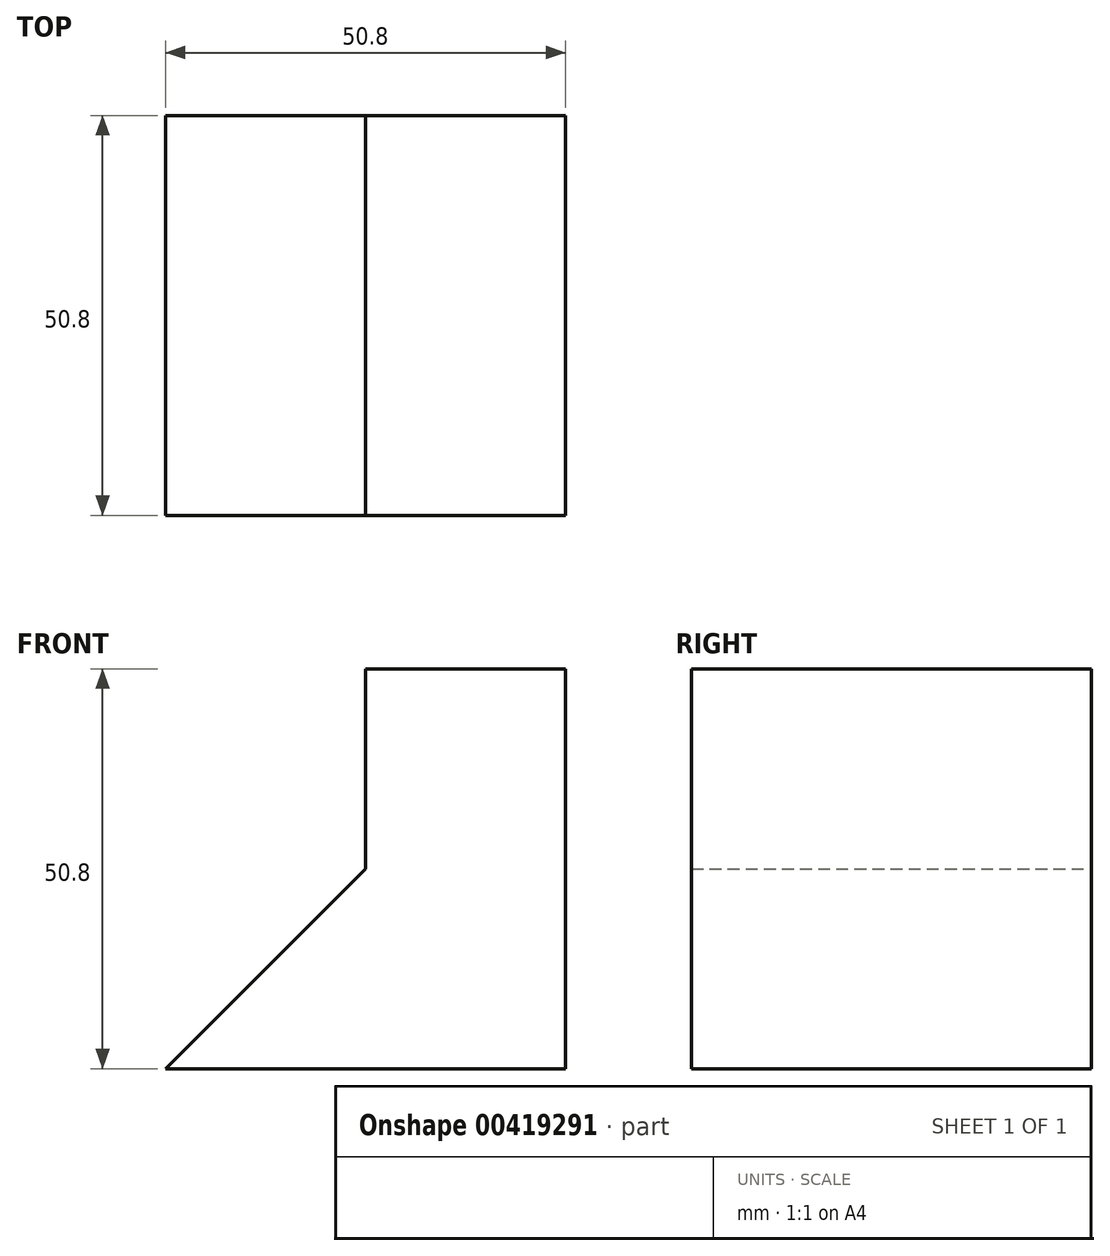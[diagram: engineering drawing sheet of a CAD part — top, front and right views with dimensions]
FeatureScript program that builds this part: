
annotation { "Feature Type Name" : "Feature", "Feature Type Description" : "" }
export const myFeature = defineFeature(function(context is Context, id is Id, definition is map)
    precondition{}
    {
        {
            var Q0;
            Q0=qCreatedBy(makeId("Front.planeOp"),FACE);
            var sketch = newSketch(context, id + "F0", { "sketchPlane" : qUnion([Q0])});
            skLineSegment(sketch, "E0", {"start": v(-50.8, 0) * mm, "end": v(0, 0) * mm});
            skLineSegment(sketch, "E1", {"start": v(0, 0) * mm, "end": v(0, 50.8) * mm});
            skLineSegment(sketch, "E2", {"start": v(0, 50.8) * mm, "end": v(-25.4, 50.8) * mm});
            skLineSegment(sketch, "E3", {"start": v(-25.4, 50.8) * mm, "end": v(-25.4, 25.4) * mm});
            skLineSegment(sketch, "E4", {"start": v(-25.4, 25.4) * mm, "end": v(-50.8, 0) * mm});
            skSolve(sketch);
        }
        {
            var Q0;
            Q0=makeQuery(id+"F0.imprint","IMPRINT",FACE,{"disambiguationData":[TD([[makeQuery(id+"F0.imprint","IMPRINT",EDGE,{"derivedFrom":sQuery(id+"F0.wireOp",EDGE,"E0")}),1.0]])]});
            extrude(context, id + "F1", {"entities" : qUnion([Q0]), "depth" : 50.8 * mm});
        }
    });
